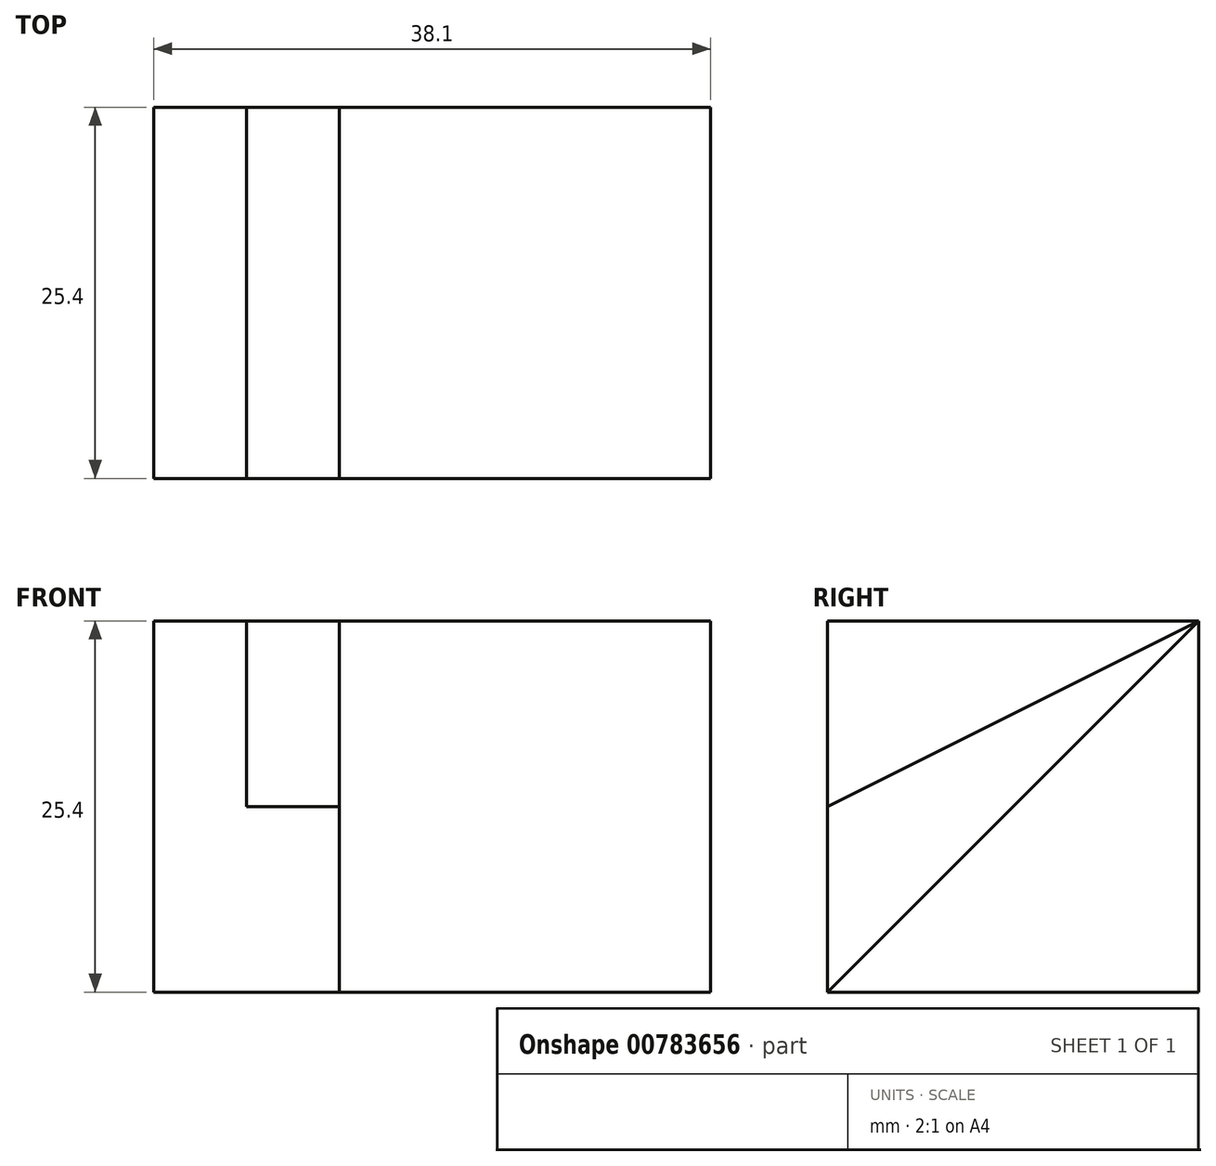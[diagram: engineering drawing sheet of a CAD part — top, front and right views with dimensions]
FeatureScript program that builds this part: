
annotation { "Feature Type Name" : "Feature", "Feature Type Description" : "" }
export const myFeature = defineFeature(function(context is Context, id is Id, definition is map)
    precondition{}
    {
        {
            var Q0;
            Q0=qCreatedBy(makeId("Front.planeOp"),FACE);
            var sketch = newSketch(context, id + "F0", { "sketchPlane" : qUnion([Q0])});
            skLineSegment(sketch, "E0", {"start": v(0, 0) * mm, "end": v(38.1, 0) * mm});
            skLineSegment(sketch, "E1", {"start": v(38.1, 0) * mm, "end": v(38.1, 25.4) * mm});
            skLineSegment(sketch, "E2", {"start": v(38.1, 25.4) * mm, "end": v(0, 25.4) * mm});
            skLineSegment(sketch, "E3", {"start": v(0, 25.4) * mm, "end": v(0, 0) * mm});
            skSolve(sketch);
        }
        {
            var Q0;
            Q0=makeQuery(id+"F0.imprint","IMPRINT",FACE,{"disambiguationData":[TD([[makeQuery(id+"F0.imprint","IMPRINT",EDGE,{"derivedFrom":sQuery(id+"F0.wireOp",EDGE,"E0")}),1.0]])]});
            extrude(context, id + "F1", {"entities" : qUnion([Q0]), "depth" : 25.4 * mm, "offsetDistance" : 25.4 * mm});
        }
        {
            var Q0;
            Q0=makeQuery(id+"F1.opExtrude","SWEPT_FACE",FACE,{"disambiguationData":[OSD([sQuery(id+"F0.wireOp",EDGE,"E1")])]});
            var sketch = newSketch(context, id + "F2", { "sketchPlane" : qUnion([Q0])});
            skLineSegment(sketch, "E4", {"start": v(-25.4, 0) * mm, "end": v(0, 25.4) * mm});
            skLineSegment(sketch, "E5", {"start": v(0, 25.4) * mm, "end": v(0, 0) * mm});
            skLineSegment(sketch, "E6", {"start": v(0, 0) * mm, "end": v(-25.4, 0) * mm});
            skSolve(sketch);
        }
        {
            var Q0;
            Q0=makeQuery(id+"F2.imprint","IMPRINT",FACE,{"disambiguationData":[TD([[makeQuery(id+"F2.imprint","IMPRINT",EDGE,{"derivedFrom":sQuery(id+"F2.wireOp",EDGE,"E4")}),1.0]])]});
            extrude(context, id + "F3", {"entities" : qUnion([Q0]), "operationType" : NewBodyOperationType.REMOVE, "oppositeDirection" : true, "depth" : 25.4 * mm, "offsetDistance" : 25.4 * mm});
        }
        {
            var Q0;
            Q0=makeQuery(id+"F3.boolean.opBoolean","COPY",FACE,{"derivedFrom":makeQuery(id+"F3.opExtrude","CAP_FACE",FACE,{"disambiguationData":[OSD([sQuery(id+"F0.wireOp",EDGE,"E1"),sQuery(id+"F0.wireOp",EDGE,"E2"),sQuery(id+"F2.wireOp",EDGE,"E4")])],"isStart":false})});
            var sketch = newSketch(context, id + "F4", { "sketchPlane" : qUnion([Q0])});
            skLineSegment(sketch, "E7", {"start": v(-25.4, 12.7) * mm, "end": v(0, 25.4) * mm});
            skLineSegment(sketch, "E8", {"start": v(0, 25.4) * mm, "end": v(-25.4, 25.4) * mm});
            skLineSegment(sketch, "E9", {"start": v(-25.4, 25.4) * mm, "end": v(-25.4, 12.7) * mm});
            skSolve(sketch);
        }
        {
            var Q0;
            Q0=makeQuery(id+"F4.imprint","IMPRINT",FACE,{"disambiguationData":[TD([[makeQuery(id+"F4.imprint","IMPRINT",EDGE,{"derivedFrom":sQuery(id+"F4.wireOp",EDGE,"E7")}),1.0]])]});
            extrude(context, id + "F5", {"entities" : qUnion([Q0]), "operationType" : NewBodyOperationType.REMOVE, "oppositeDirection" : true, "depth" : 6.35 * mm, "offsetDistance" : 25.4 * mm});
        }
    });
